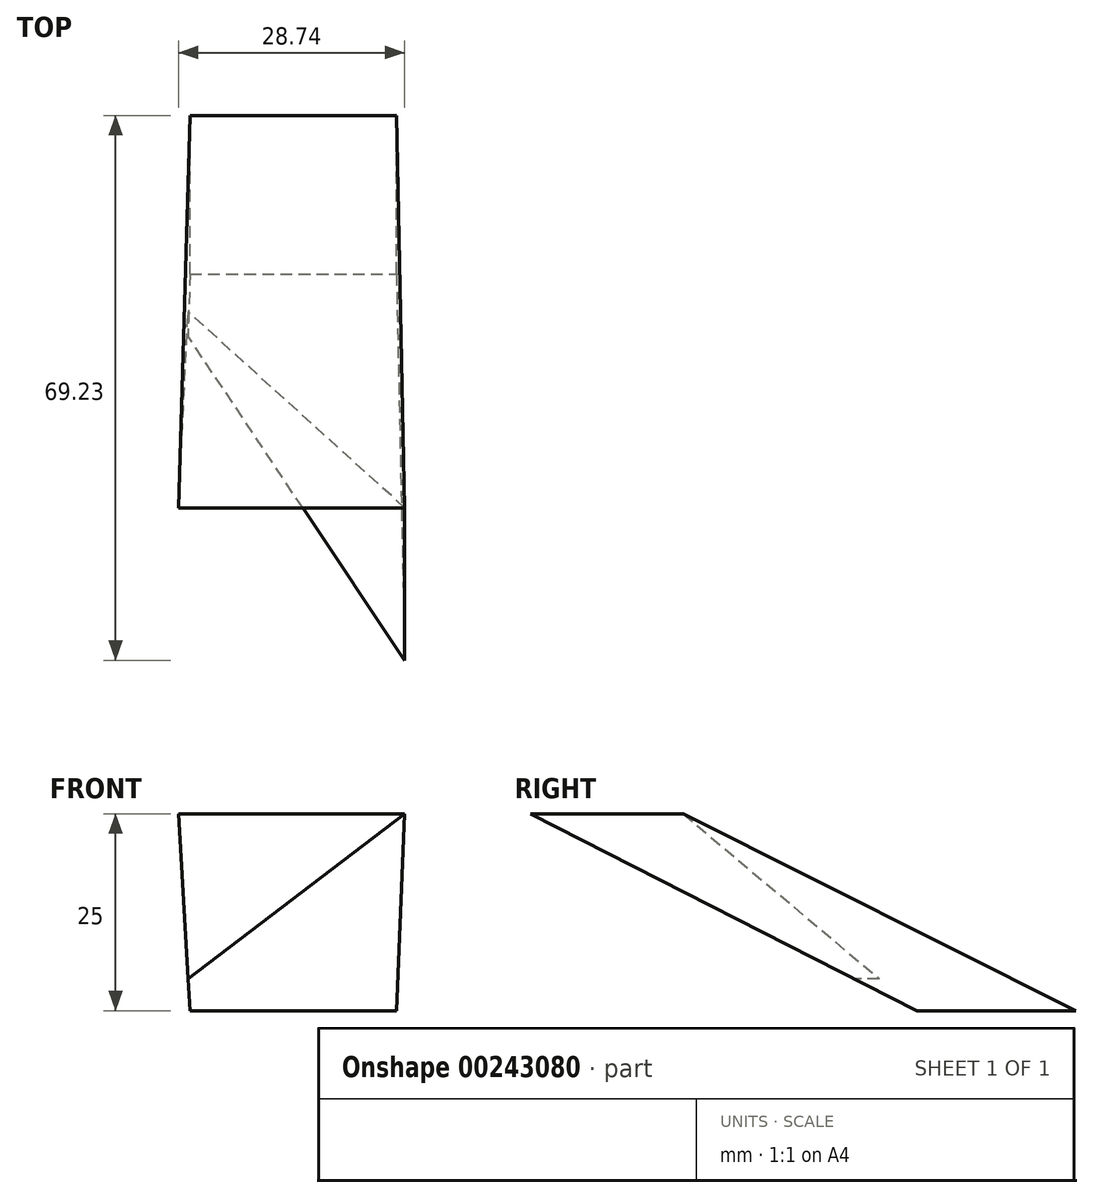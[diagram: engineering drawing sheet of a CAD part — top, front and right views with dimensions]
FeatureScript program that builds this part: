
annotation { "Feature Type Name" : "Feature", "Feature Type Description" : "" }
export const myFeature = defineFeature(function(context is Context, id is Id, definition is map)
    precondition{}
    {
        {
            var Q0;
            Q0=qCreatedBy(makeId("Top.planeOp"),FACE);
            var sketch = newSketch(context, id + "F0", { "sketchPlane" : qUnion([Q0])});
            skLineSegment(sketch, "E0.bottom", {"start": v(5.5, 0) * mm, "end": v(31.75, 0) * mm});
            skLineSegment(sketch, "E0.top", {"start": v(5.5, 20.15) * mm, "end": v(31.75, 20.15) * mm});
            skLineSegment(sketch, "E0.left", {"start": v(5.5, 0) * mm, "end": v(5.5, 20.15) * mm});
            skLineSegment(sketch, "E0.right", {"start": v(31.75, 0) * mm, "end": v(31.75, 20.15) * mm});
            skSolve(sketch);
        }
        {
            var Q0;
            Q0=qCreatedBy(makeId("Top.planeOp"),FACE);
            cPlane(context, id + "F1", {"entities" : qUnion([Q0]), "cplaneType" : CPlaneType.OFFSET, "offset" : 25 * mm, "width" : 150 * mm, "height" : 150 * mm});
        }
        {
            var Q0;
            Q0=qCreatedBy(id+"F1.planeOp",FACE);
            var sketch = newSketch(context, id + "F2", { "sketchPlane" : qUnion([Q0])});
            skLineSegment(sketch, "E1.bottom", {"start": v(32.8, -49.08) * mm, "end": v(4.06, -49.08) * mm});
            skLineSegment(sketch, "E1.top", {"start": v(32.8, -29.7) * mm, "end": v(4.06, -29.7) * mm});
            skLineSegment(sketch, "E1.left", {"start": v(32.8, -49.08) * mm, "end": v(32.8, -29.7) * mm});
            skLineSegment(sketch, "E1.right", {"start": v(4.06, -49.08) * mm, "end": v(4.06, -29.7) * mm});
            skSolve(sketch);
        }
        {
            var Q0;
            Q0=makeQuery(id+"F0.imprint","IMPRINT",FACE,{"disambiguationData":[TD([[makeQuery(id+"F0.imprint","IMPRINT",EDGE,{"derivedFrom":sQuery(id+"F0.wireOp",EDGE,"E0.bottom")}),1.0]])]});
            var Q1;
            Q1=makeQuery(id+"F2.imprint","IMPRINT",FACE,{"disambiguationData":[TD([[makeQuery(id+"F2.imprint","IMPRINT",EDGE,{"derivedFrom":sQuery(id+"F2.wireOp",EDGE,"E1.bottom")}),-1.0]])]});
            loft(context, id + "F3", {"sheetProfilesArray" : [{ "sheetProfileEntities" : qUnion([Q0]) }, { "sheetProfileEntities" : qUnion([Q1]) }]});
        }
        {
            var Q1;
            Q1=makeQuery(id+"F3.opLoft","CAP_FACE",FACE,{"disambiguationData":[OSD([makeQuery(id+"F2.imprint","IMPRINT",FACE,{"disambiguationData":[TD([[makeQuery(id+"F2.imprint","IMPRINT",EDGE,{"derivedFrom":sQuery(id+"F2.wireOp",EDGE,"E1.bottom")}),-1.0]])]})])],"isStart":true});
            var Q2;
            Q2=qCreatedBy(makeId("Origin.pointOp"),VERTEX);
            loft(context, id + "F4", {"operationType" : NewBodyOperationType.REMOVE, "sheetProfilesArray" : [{ "sheetProfileEntities" : qUnion([Q1]) }, { "sheetProfileEntities" : qUnion([Q2]) }]});
        }
    });
